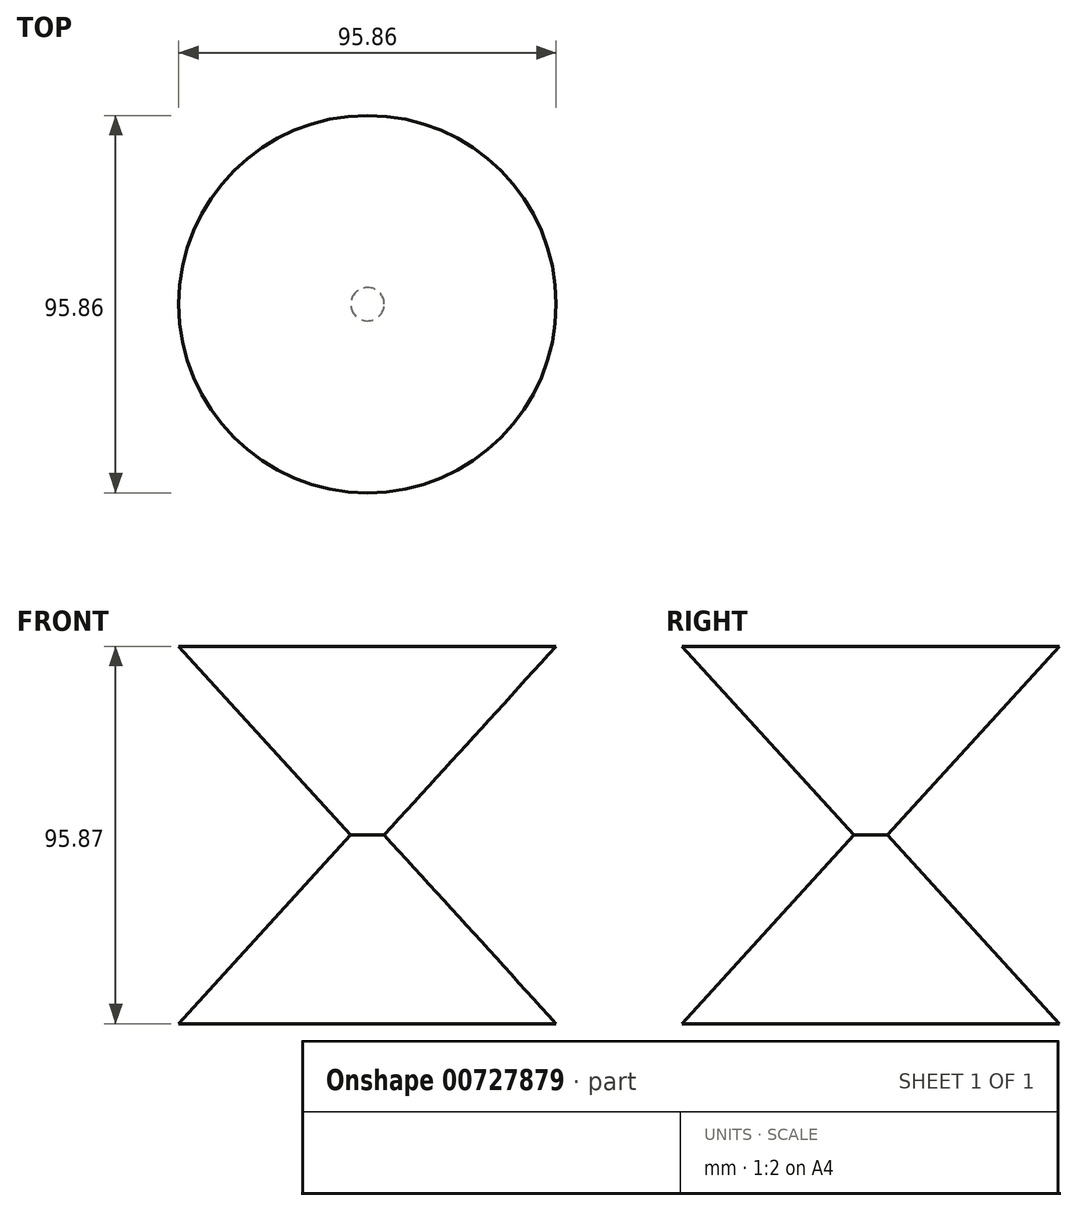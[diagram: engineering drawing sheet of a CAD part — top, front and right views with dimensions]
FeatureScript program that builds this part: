
annotation { "Feature Type Name" : "Feature", "Feature Type Description" : "" }
export const myFeature = defineFeature(function(context is Context, id is Id, definition is map)
    precondition{}
    {
        {
            var Q0;
            Q0=qCreatedBy(makeId("Right.planeOp"),FACE);
            var sketch = newSketch(context, id + "F0", { "sketchPlane" : qUnion([Q0])});
            skLineSegment(sketch, "E0", {"start": v(0, 0) * mm, "end": v(0, 95.87) * mm, "construction": true});
            skLineSegment(sketch, "E1", {"start": v(0, 95.87) * mm, "end": v(47.93, 95.87) * mm});
            skLineSegment(sketch, "E2", {"start": v(47.93, 95.87) * mm, "end": v(4.24, 47.94) * mm});
            skLineSegment(sketch, "E3", {"start": v(4.24, 47.94) * mm, "end": v(47.93, 0) * mm});
            skLineSegment(sketch, "E4", {"start": v(47.93, 0) * mm, "end": v(0, 0) * mm});
            skSolve(sketch);
        }
        {
            var Q0;
            Q0=sQuery(id+"F0.wireOp",EDGE,"E1");
            var Q1;
            Q1=sQuery(id+"F0.wireOp",EDGE,"E2");
            var Q2;
            Q2=sQuery(id+"F0.wireOp",EDGE,"E3");
            var Q3;
            Q3=sQuery(id+"F0.wireOp",EDGE,"E4");
            var Q4;
            Q4=sQuery(id+"F0.wireOp",EDGE,"E0");
            revolve(context, id + "F1", {"bodyType" : ToolBodyType.SURFACE, "surfaceOperationType" : NewSurfaceOperationType.NEW, "surfaceEntities" : qUnion([Q0, Q1, Q2, Q3]), "axis" : qUnion([Q4]), "revolveType" : RevolveType.FULL});
        }
    });
